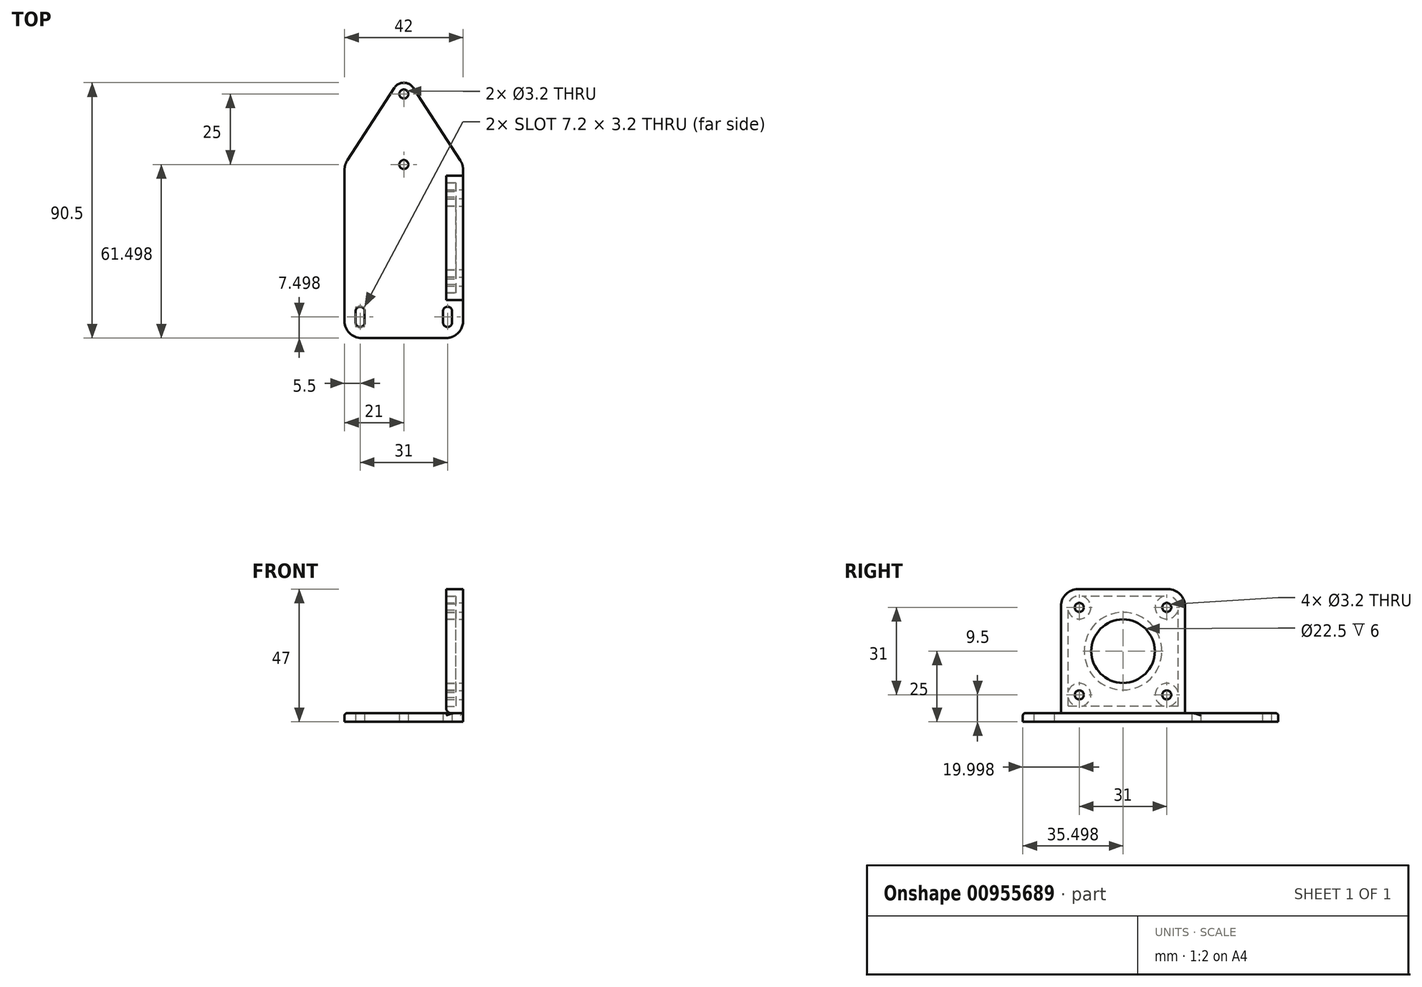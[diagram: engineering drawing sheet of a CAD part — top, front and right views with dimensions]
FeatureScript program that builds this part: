
annotation { "Feature Type Name" : "Feature", "Feature Type Description" : "" }
export const myFeature = defineFeature(function(context is Context, id is Id, definition is map)
    precondition{}
    {
        {
            var Q0;
            Q0=qCreatedBy(makeId("Top.planeOp"),FACE);
            var sketch = newSketch(context, id + "F0", { "sketchPlane" : qUnion([Q0])});
            skCircle(sketch, "E0", {"center": v(0, 35.34) * mm, "radius": 1.6 * mm});
            skLineSegment(sketch, "E1", {"start": v(-15.5, -16.66) * mm, "end": v(15.5, -16.66) * mm, "construction": true});
            skArc(sketch, "E2", {"start": v(-13.9, -16.66) * mm, "mid": v(-15.5, -15.06) * mm, "end": v(-17.1, -16.66) * mm});
            skArc(sketch, "E3", {"start": v(17.1, -16.66) * mm, "mid": v(15.5, -15.06) * mm, "end": v(13.9, -16.66) * mm});
            skLineSegment(sketch, "E4", {"start": v(-15.5, -16.66) * mm, "end": v(-15.5, -20.66) * mm, "construction": true});
            skLineSegment(sketch, "E5", {"start": v(15.5, -16.66) * mm, "end": v(15.5, -20.66) * mm, "construction": true});
            skArc(sketch, "E6", {"start": v(-17.1, -20.66) * mm, "mid": v(-15.5, -22.26) * mm, "end": v(-13.9, -20.66) * mm});
            skArc(sketch, "E7", {"start": v(13.9, -20.66) * mm, "mid": v(15.5, -22.26) * mm, "end": v(17.1, -20.66) * mm});
            skLineSegment(sketch, "E8", {"start": v(-17.1, -16.66) * mm, "end": v(-17.1, -20.66) * mm});
            skLineSegment(sketch, "E9", {"start": v(-13.9, -16.66) * mm, "end": v(-13.9, -20.66) * mm});
            skLineSegment(sketch, "E10", {"start": v(13.9, -16.66) * mm, "end": v(13.9, -20.66) * mm});
            skLineSegment(sketch, "E11", {"start": v(17.1, -16.66) * mm, "end": v(17.1, -20.66) * mm});
            skLineSegment(sketch, "E12.bottom", {"start": v(-21, 35.34) * mm, "end": v(21, 35.34) * mm, "construction": true});
            skLineSegment(sketch, "E12.top", {"start": v(-21, -26.16) * mm, "end": v(21, -26.16) * mm});
            skLineSegment(sketch, "E12.left", {"start": v(-21, 35.34) * mm, "end": v(-21, -26.16) * mm});
            skLineSegment(sketch, "E12.right", {"start": v(21, 35.34) * mm, "end": v(21, -26.16) * mm});
            skPoint(sketch, "E13", {"position": v(0, -16.66) * mm});
            skPoint(sketch, "E14", {"position": v(0, -26.16) * mm});
            skLineSegment(sketch, "E15", {"start": v(-15.5, -16.66) * mm, "end": v(-21, -16.66) * mm, "construction": true});
            skLineSegment(sketch, "E16", {"start": v(-15.5, -20.66) * mm, "end": v(-15.5, -26.16) * mm, "construction": true});
            skCircle(sketch, "E17", {"center": v(0, 60.34) * mm, "radius": 1.6 * mm});
            skArc(sketch, "E18", {"start": v(3.35, 62.52) * mm, "mid": v(0, 64.34) * mm, "end": v(-3.35, 62.52) * mm});
            skLineSegment(sketch, "E19", {"start": v(-21, 35.34) * mm, "end": v(-3.35, 62.52) * mm});
            skLineSegment(sketch, "E20", {"start": v(21, 35.34) * mm, "end": v(3.35, 62.52) * mm});
            skLineSegment(sketch, "E21", {"start": v(0, 60.34) * mm, "end": v(0, 35.34) * mm, "construction": true});
            skPoint(sketch, "E22", {"position": v(0, 47.84) * mm});
            skCircle(sketch, "E23", {"center": v(0, 47.84) * mm, "radius": 6.5 * mm, "construction": true});
            skSolve(sketch);
        }
        {
            var Q0;
            Q0 = qSketchRegion(id + "F0", true);
            extrude(context, id + "F1", {"entities" : qUnion([Q0]), "depth" : 3 * mm, "offsetDistance" : 25 * mm});
        }
        {
            var Q0;
            Q0=makeQuery(id+"F1.opExtrude","SWEPT_FACE",FACE,{"disambiguationData":[OSD([sQuery(id+"F0.wireOp",EDGE,"E12.right")])]});
            var sketch = newSketch(context, id + "F2", { "sketchPlane" : qUnion([Q0])});
            skLineSegment(sketch, "E24", {"start": v(31.34, 3) * mm, "end": v(31.34, 47) * mm});
            skLineSegment(sketch, "E25", {"start": v(31.34, 47) * mm, "end": v(-12.66, 47) * mm});
            skLineSegment(sketch, "E26", {"start": v(-12.66, 47) * mm, "end": v(-12.66, 3) * mm});
            skLineSegment(sketch, "E27.0", {"start": v(35.34, 3) * mm, "end": v(-26.16, 3) * mm});
            skPoint(sketch, "E28.0", {"position": v(-16.66, 0) * mm});
            skLineSegment(sketch, "E29", {"start": v(35.34, 3) * mm, "end": v(-16.66, 3) * mm, "construction": true});
            skLineSegment(sketch, "E30", {"start": v(31.34, 3) * mm, "end": v(-12.66, 3) * mm, "construction": true});
            skPoint(sketch, "E31", {"position": v(9.34, 3) * mm});
            skPoint(sketch, "E32.positionSnap0", {"position": v(9.34, 47) * mm});
            skLineSegment(sketch, "E33", {"start": v(9.34, 47) * mm, "end": v(9.34, 3) * mm, "construction": true});
            skPoint(sketch, "E34", {"position": v(9.34, 25) * mm});
            skCircle(sketch, "E35", {"center": v(9.34, 25) * mm, "radius": 11.25 * mm});
            skLineSegment(sketch, "E36.bottom", {"start": v(-6.16, 40.5) * mm, "end": v(24.84, 40.5) * mm, "construction": true});
            skLineSegment(sketch, "E36.top", {"start": v(-6.16, 9.5) * mm, "end": v(24.84, 9.5) * mm, "construction": true});
            skLineSegment(sketch, "E36.left", {"start": v(-6.16, 40.5) * mm, "end": v(-6.16, 9.5) * mm, "construction": true});
            skLineSegment(sketch, "E36.right", {"start": v(24.84, 40.5) * mm, "end": v(24.84, 9.5) * mm, "construction": true});
            skCircle(sketch, "E37", {"center": v(24.84, 40.5) * mm, "radius": 1.6 * mm});
            skCircle(sketch, "E38", {"center": v(-6.16, 40.5) * mm, "radius": 1.6 * mm});
            skCircle(sketch, "E39", {"center": v(-6.16, 9.5) * mm, "radius": 1.6 * mm});
            skCircle(sketch, "E40", {"center": v(24.84, 9.5) * mm, "radius": 1.6 * mm});
            skCircle(sketch, "E41", {"center": v(24.84, 40.5) * mm, "radius": 6.5 * mm, "construction": true});
            skSolve(sketch);
        }
        {
            var Q0;
            Q0 = qSketchRegion(id + "F2", true);
            extrude(context, id + "F3", {"entities" : qUnion([Q0]), "oppositeDirection" : true, "depth" : 6 * mm, "offsetDistance" : 25 * mm});
        }
        {
            var Q0;
            Q0=makeQuery(id+"F1.opExtrude","SWEPT_EDGE",EDGE,{"disambiguationData":[OSD([sQuery(id+"F0.wireOp",EDGE,"E12.right"),sQuery(id+"F0.wireOp",EDGE,"E20")])]});
            var Q1;
            Q1=makeQuery(id+"F1.opExtrude","SWEPT_EDGE",EDGE,{"disambiguationData":[OSD([sQuery(id+"F0.wireOp",EDGE,"E12.top"),sQuery(id+"F0.wireOp",EDGE,"E12.left")])]});
            var Q2;
            Q2=makeQuery(id+"F1.opExtrude","SWEPT_EDGE",EDGE,{"disambiguationData":[OSD([sQuery(id+"F0.wireOp",EDGE,"E12.left"),sQuery(id+"F0.wireOp",EDGE,"E19")])]});
            var Q3;
            Q3=makeQuery(id+"F1.opExtrude","SWEPT_EDGE",EDGE,{"disambiguationData":[OSD([sQuery(id+"F0.wireOp",EDGE,"E12.top"),sQuery(id+"F0.wireOp",EDGE,"E12.right")])]});
            var Q4;
            Q4=makeQuery(id+"F3.opExtrude","SWEPT_EDGE",EDGE,{"disambiguationData":[OSD([sQuery(id+"F2.wireOp",EDGE,"E25"),sQuery(id+"F2.wireOp",EDGE,"E26")])]});
            var Q5;
            Q5=makeQuery(id+"F3.opExtrude","SWEPT_EDGE",EDGE,{"disambiguationData":[OSD([sQuery(id+"F2.wireOp",EDGE,"E24"),sQuery(id+"F2.wireOp",EDGE,"E25")])]});
            fillet(context, id + "F4", {"entities" : qUnion([Q0, Q1, Q2, Q3, Q4, Q5]), "radius" : 6 * mm, "tangentPropagation" : true, "allowEdgeOverflow" : false});
        }
        {
            var Q0;
            Q0=makeQuery(id+"F1.opExtrude","CAP_EDGE",EDGE,{"disambiguationData":[OSD([sQuery(id+"F0.wireOp",EDGE,"E12.left")])],"isStart":false});
            var Q1;
            Q1=makeQuery(id+"F1.opExtrude","CAP_EDGE",EDGE,{"disambiguationData":[OSD([sQuery(id+"F0.wireOp",EDGE,"E12.top")])],"isStart":false});
            var Q2;
            {var subQ0=sQuery(id+"F0.wireOp",EDGE,"E19");var subQ1=sQuery(id+"F0.wireOp",EDGE,"E12.left");Q2=makeQuery(id+"F4.opFillet","BLEND_EDGE",EDGE,{"blendedFrom":[makeQuery(id+"F1.opExtrude","SWEPT_EDGE",EDGE,{"disambiguationData":[OSD([subQ1,subQ0])]}),makeQuery(id+"F1.opExtrude","CAP_FACE",FACE,{"disambiguationData":[OSD([sQuery(id+"F0.wireOp",EDGE,"E0"),sQuery(id+"F0.wireOp",EDGE,"E2"),sQuery(id+"F0.wireOp",EDGE,"E3"),sQuery(id+"F0.wireOp",EDGE,"E6"),sQuery(id+"F0.wireOp",EDGE,"E7"),sQuery(id+"F0.wireOp",EDGE,"E8"),sQuery(id+"F0.wireOp",EDGE,"E9"),sQuery(id+"F0.wireOp",EDGE,"E10"),sQuery(id+"F0.wireOp",EDGE,"E11"),sQuery(id+"F0.wireOp",EDGE,"E12.top"),subQ1,sQuery(id+"F0.wireOp",EDGE,"E12.right"),sQuery(id+"F0.wireOp",EDGE,"E17"),sQuery(id+"F0.wireOp",EDGE,"E18"),subQ0,sQuery(id+"F0.wireOp",EDGE,"E20")])],"isStart":false})],"blendedInto":[makeQuery(id+"F1.opExtrude","CAP_FACE",FACE,{"disambiguationData":[OSD([sQuery(id+"F0.wireOp",EDGE,"E0"),sQuery(id+"F0.wireOp",EDGE,"E2"),sQuery(id+"F0.wireOp",EDGE,"E3"),sQuery(id+"F0.wireOp",EDGE,"E6"),sQuery(id+"F0.wireOp",EDGE,"E7"),sQuery(id+"F0.wireOp",EDGE,"E8"),sQuery(id+"F0.wireOp",EDGE,"E9"),sQuery(id+"F0.wireOp",EDGE,"E10"),sQuery(id+"F0.wireOp",EDGE,"E11"),sQuery(id+"F0.wireOp",EDGE,"E12.top"),subQ1,sQuery(id+"F0.wireOp",EDGE,"E12.right"),sQuery(id+"F0.wireOp",EDGE,"E17"),sQuery(id+"F0.wireOp",EDGE,"E18"),subQ0,sQuery(id+"F0.wireOp",EDGE,"E20")])],"isStart":false})]});}
            var Q3;
            Q3=makeQuery(id+"F1.opExtrude","CAP_EDGE",EDGE,{"disambiguationData":[OSD([sQuery(id+"F0.wireOp",EDGE,"E19")])],"isStart":false});
            var Q4;
            Q4=makeQuery(id+"F1.opExtrude","CAP_EDGE",EDGE,{"disambiguationData":[OSD([sQuery(id+"F0.wireOp",EDGE,"E18")])],"isStart":false});
            var Q5;
            Q5=makeQuery(id+"F1.opExtrude","CAP_EDGE",EDGE,{"disambiguationData":[OSD([sQuery(id+"F0.wireOp",EDGE,"E20")])],"isStart":false});
            var Q6;
            {var subQ0=sQuery(id+"F0.wireOp",EDGE,"E12.left");var subQ1=sQuery(id+"F0.wireOp",EDGE,"E12.top");Q6=makeQuery(id+"F4.opFillet","BLEND_EDGE",EDGE,{"blendedFrom":[makeQuery(id+"F1.opExtrude","SWEPT_EDGE",EDGE,{"disambiguationData":[OSD([subQ1,subQ0])]}),makeQuery(id+"F1.opExtrude","CAP_FACE",FACE,{"disambiguationData":[OSD([sQuery(id+"F0.wireOp",EDGE,"E0"),sQuery(id+"F0.wireOp",EDGE,"E2"),sQuery(id+"F0.wireOp",EDGE,"E3"),sQuery(id+"F0.wireOp",EDGE,"E6"),sQuery(id+"F0.wireOp",EDGE,"E7"),sQuery(id+"F0.wireOp",EDGE,"E8"),sQuery(id+"F0.wireOp",EDGE,"E9"),sQuery(id+"F0.wireOp",EDGE,"E10"),sQuery(id+"F0.wireOp",EDGE,"E11"),subQ1,subQ0,sQuery(id+"F0.wireOp",EDGE,"E12.right"),sQuery(id+"F0.wireOp",EDGE,"E17"),sQuery(id+"F0.wireOp",EDGE,"E18"),sQuery(id+"F0.wireOp",EDGE,"E19"),sQuery(id+"F0.wireOp",EDGE,"E20")])],"isStart":false})],"blendedInto":[makeQuery(id+"F1.opExtrude","CAP_FACE",FACE,{"disambiguationData":[OSD([sQuery(id+"F0.wireOp",EDGE,"E0"),sQuery(id+"F0.wireOp",EDGE,"E2"),sQuery(id+"F0.wireOp",EDGE,"E3"),sQuery(id+"F0.wireOp",EDGE,"E6"),sQuery(id+"F0.wireOp",EDGE,"E7"),sQuery(id+"F0.wireOp",EDGE,"E8"),sQuery(id+"F0.wireOp",EDGE,"E9"),sQuery(id+"F0.wireOp",EDGE,"E10"),sQuery(id+"F0.wireOp",EDGE,"E11"),subQ1,subQ0,sQuery(id+"F0.wireOp",EDGE,"E12.right"),sQuery(id+"F0.wireOp",EDGE,"E17"),sQuery(id+"F0.wireOp",EDGE,"E18"),sQuery(id+"F0.wireOp",EDGE,"E19"),sQuery(id+"F0.wireOp",EDGE,"E20")])],"isStart":false})]});}
            fillet(context, id + "F5", {"entities" : qUnion([Q0, Q1, Q2, Q3, Q4, Q5, Q6]), "radius" : 0.8 * mm, "allowEdgeOverflow" : false});
        }
        {
            var Q0;
            Q0=makeQuery(id+"F3.opExtrude","CAP_FACE",FACE,{"disambiguationData":[OSD([sQuery(id+"F2.wireOp",EDGE,"E24"),sQuery(id+"F2.wireOp",EDGE,"E25"),sQuery(id+"F2.wireOp",EDGE,"E26"),sQuery(id+"F2.wireOp",EDGE,"E27.0"),sQuery(id+"F2.wireOp",EDGE,"E35"),sQuery(id+"F2.wireOp",EDGE,"E37"),sQuery(id+"F2.wireOp",EDGE,"E38"),sQuery(id+"F2.wireOp",EDGE,"E39"),sQuery(id+"F2.wireOp",EDGE,"E40")])],"isStart":false});
            var Q1;
            Q1=makeQuery(id+"F3.opExtrude","SWEPT_BODY",BODY,{"disambiguationData":[OSD([sQuery(id+"F2.wireOp",EDGE,"E24"),sQuery(id+"F2.wireOp",EDGE,"E25"),sQuery(id+"F2.wireOp",EDGE,"E26"),sQuery(id+"F2.wireOp",EDGE,"E27.0"),sQuery(id+"F2.wireOp",EDGE,"E35"),sQuery(id+"F2.wireOp",EDGE,"E37"),sQuery(id+"F2.wireOp",EDGE,"E38"),sQuery(id+"F2.wireOp",EDGE,"E39"),sQuery(id+"F2.wireOp",EDGE,"E40")])]});
            shell(context, id + "F6", {"entities" : qUnion([Q0]), "parts" : qUnion([Q1]), "thickness" : 2.5 * mm});
        }
        {
            var Q0;
            Q0=makeQuery(id+"F3.opExtrude","CAP_EDGE",EDGE,{"disambiguationData":[OSD([sQuery(id+"F2.wireOp",EDGE,"E27.0")])],"isStart":false});
            fillet(context, id + "F7", {"entities" : qUnion([Q0]), "radius" : 2 * mm, "tangentPropagation" : true, "allowEdgeOverflow" : false});
        }
    });
